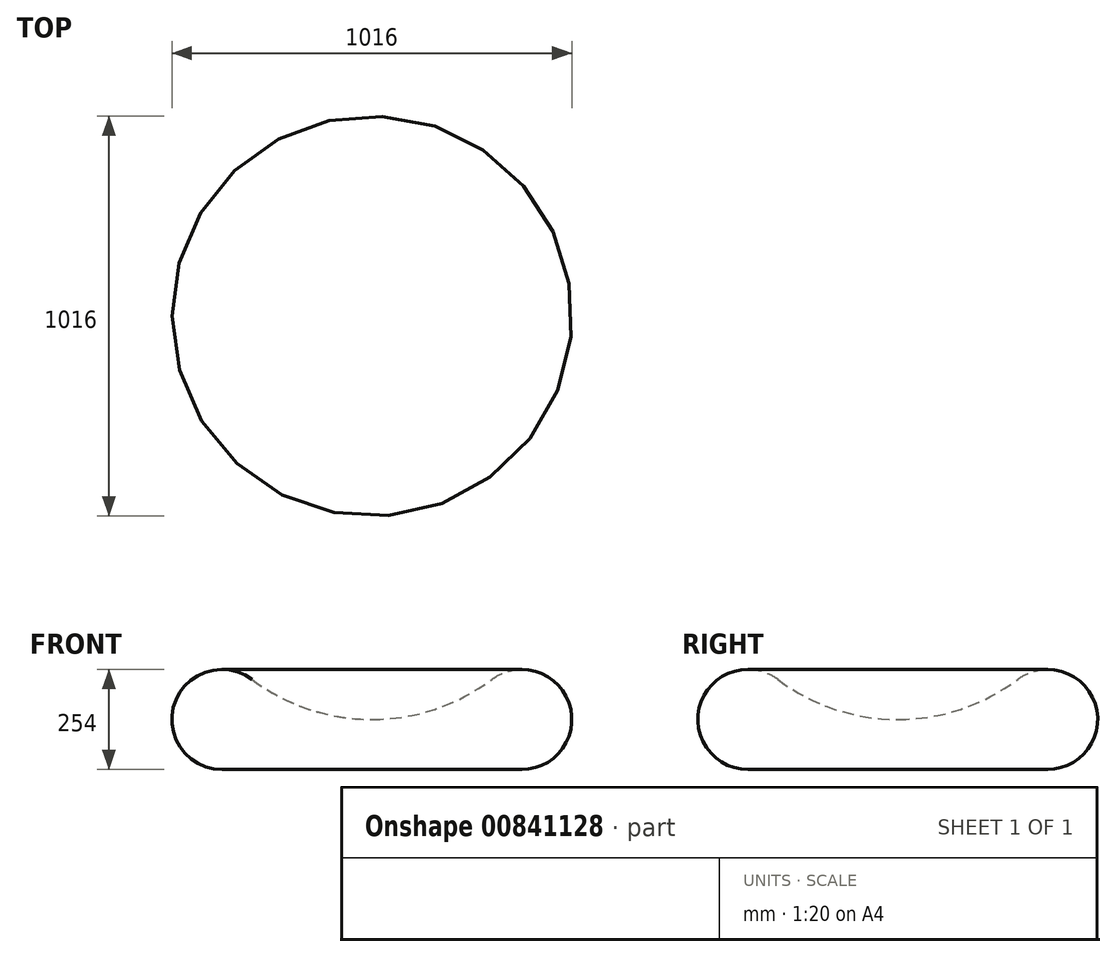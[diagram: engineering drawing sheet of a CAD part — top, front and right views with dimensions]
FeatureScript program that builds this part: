
annotation { "Feature Type Name" : "Feature", "Feature Type Description" : "" }
export const myFeature = defineFeature(function(context is Context, id is Id, definition is map)
    precondition{}
    {
        {
            var Q0;
            Q0=qCreatedBy(makeId("Front.planeOp"),FACE);
            var sketch = newSketch(context, id + "F0", { "sketchPlane" : qUnion([Q0])});
            skArc(sketch, "E0", {"start": v(-304.8, 228.6) * mm, "mid": v(-501.48, 167.16) * mm, "end": v(-381, 0) * mm});
            skArc(sketch, "E1", {"start": v(-304.8, 228.6) * mm, "mid": v(-160.64, 153.07) * mm, "end": v(0, 127) * mm});
            skLineSegment(sketch, "E2", {"start": v(0, 0) * mm, "end": v(-381, 0) * mm});
            skLineSegment(sketch, "E3", {"start": v(0, 0) * mm, "end": v(0, 127) * mm});
            skSolve(sketch);
        }
        {
            var Q0;
            Q0 = qSketchRegion(id + "F0", true);
            var Q1;
            Q1=sQuery(id+"F0.wireOp",EDGE,"E3");
            revolve(context, id + "F1", {"surfaceOperationType" : NewSurfaceOperationType.NEW, "entities" : qUnion([Q0]), "axis" : qUnion([Q1]), "revolveType" : RevolveType.FULL});
        }
    });
